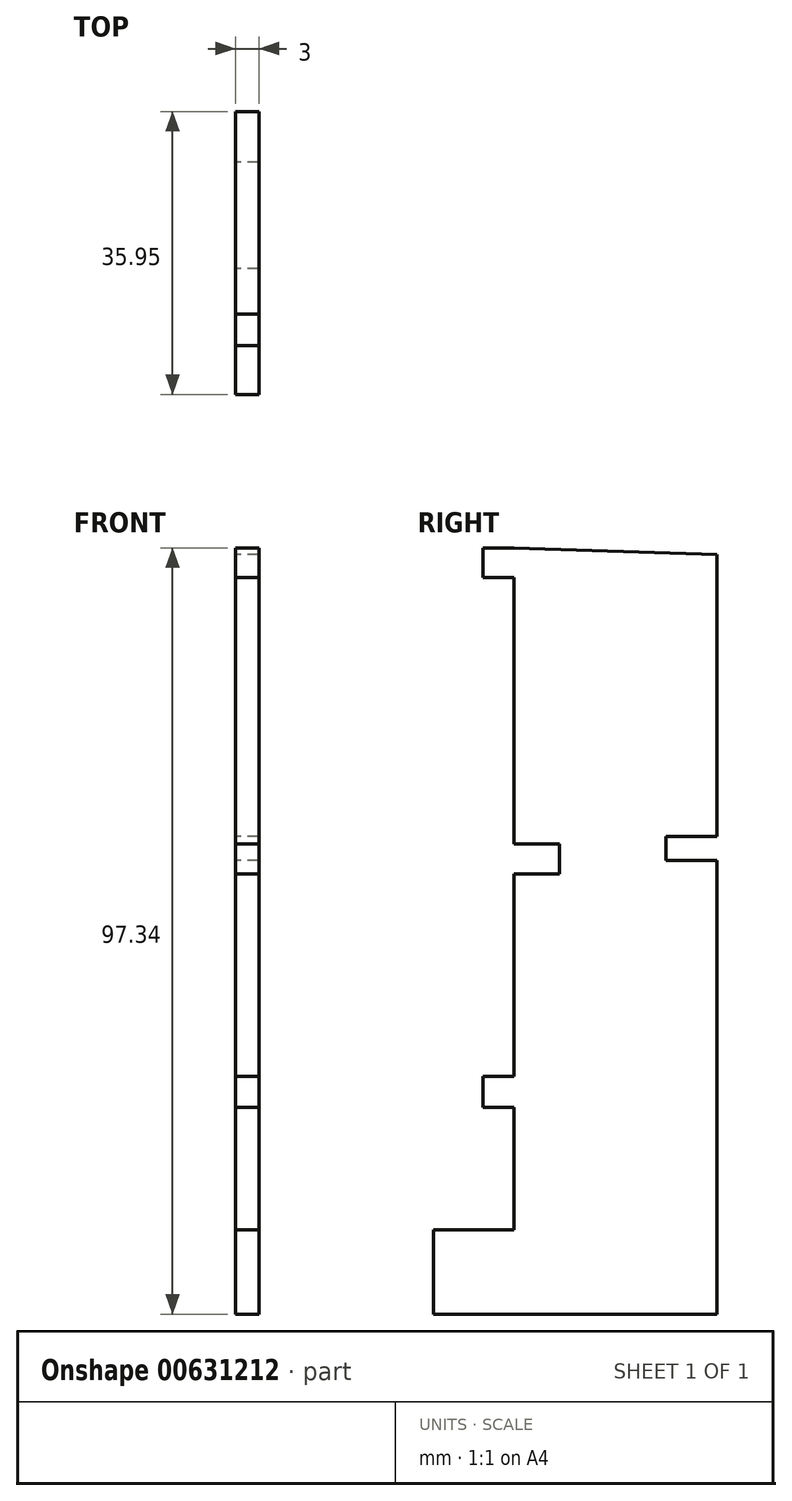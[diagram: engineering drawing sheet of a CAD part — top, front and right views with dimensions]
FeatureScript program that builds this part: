
annotation { "Feature Type Name" : "Feature", "Feature Type Description" : "" }
export const myFeature = defineFeature(function(context is Context, id is Id, definition is map)
    precondition{}
    {
        {
            var Q0;
            Q0=qCreatedBy(makeId("Right.planeOp"),FACE);
            var sketch = newSketch(context, id + "F0", { "sketchPlane" : qUnion([Q0])});
            skLineSegment(sketch, "E0", {"start": v(38.3, -19.03) * mm, "end": v(2.35, -19.03) * mm});
            skLineSegment(sketch, "E1", {"start": v(2.35, -19.03) * mm, "end": v(2.35, -8.3) * mm});
            skLineSegment(sketch, "E2", {"start": v(2.35, -8.3) * mm, "end": v(12.55, -8.3) * mm});
            skLineSegment(sketch, "E3", {"start": v(12.55, -8.3) * mm, "end": v(12.55, 7.25) * mm});
            skLineSegment(sketch, "E4", {"start": v(12.55, 7.25) * mm, "end": v(8.58, 7.25) * mm});
            skLineSegment(sketch, "E5", {"start": v(8.58, 7.25) * mm, "end": v(8.58, 11.2) * mm});
            skLineSegment(sketch, "E6", {"start": v(8.58, 11.2) * mm, "end": v(12.55, 11.2) * mm});
            skLineSegment(sketch, "E7", {"start": v(12.55, 11.2) * mm, "end": v(12.55, 36.88) * mm});
            skLineSegment(sketch, "E8", {"start": v(12.55, 36.88) * mm, "end": v(18.33, 36.88) * mm});
            skLineSegment(sketch, "E9", {"start": v(18.33, 36.88) * mm, "end": v(18.33, 40.72) * mm});
            skLineSegment(sketch, "E10", {"start": v(18.33, 40.72) * mm, "end": v(12.55, 40.72) * mm});
            skLineSegment(sketch, "E11", {"start": v(12.55, 40.72) * mm, "end": v(12.55, 74.57) * mm});
            skLineSegment(sketch, "E12", {"start": v(12.55, 74.57) * mm, "end": v(8.58, 74.57) * mm});
            skLineSegment(sketch, "E13", {"start": v(8.58, 74.57) * mm, "end": v(8.58, 78.31) * mm});
            skLineSegment(sketch, "E14", {"start": v(8.58, 78.31) * mm, "end": v(12.55, 78.31) * mm});
            skLineSegment(sketch, "E15", {"start": v(12.55, 78.31) * mm, "end": v(38.3, 77.44) * mm});
            skLineSegment(sketch, "E16", {"start": v(38.3, 77.44) * mm, "end": v(38.3, 41.68) * mm});
            skLineSegment(sketch, "E17", {"start": v(38.3, 41.68) * mm, "end": v(31.86, 41.68) * mm});
            skLineSegment(sketch, "E18", {"start": v(31.86, 41.68) * mm, "end": v(31.86, 38.59) * mm});
            skLineSegment(sketch, "E19", {"start": v(31.86, 38.59) * mm, "end": v(38.3, 38.59) * mm});
            skLineSegment(sketch, "E20", {"start": v(38.3, 38.59) * mm, "end": v(38.3, -19.03) * mm});
            skSolve(sketch);
        }
        {
            var Q0;
            Q0=makeQuery(id+"F0.imprint","IMPRINT",FACE,{"disambiguationData":[TD([[makeQuery(id+"F0.imprint","IMPRINT",EDGE,{"derivedFrom":sQuery(id+"F0.wireOp",EDGE,"E0")}),-1.0]])]});
            extrude(context, id + "F1", {"entities" : qUnion([Q0]), "depth" : 3 * mm, "offsetDistance" : 25 * mm});
        }
    });
